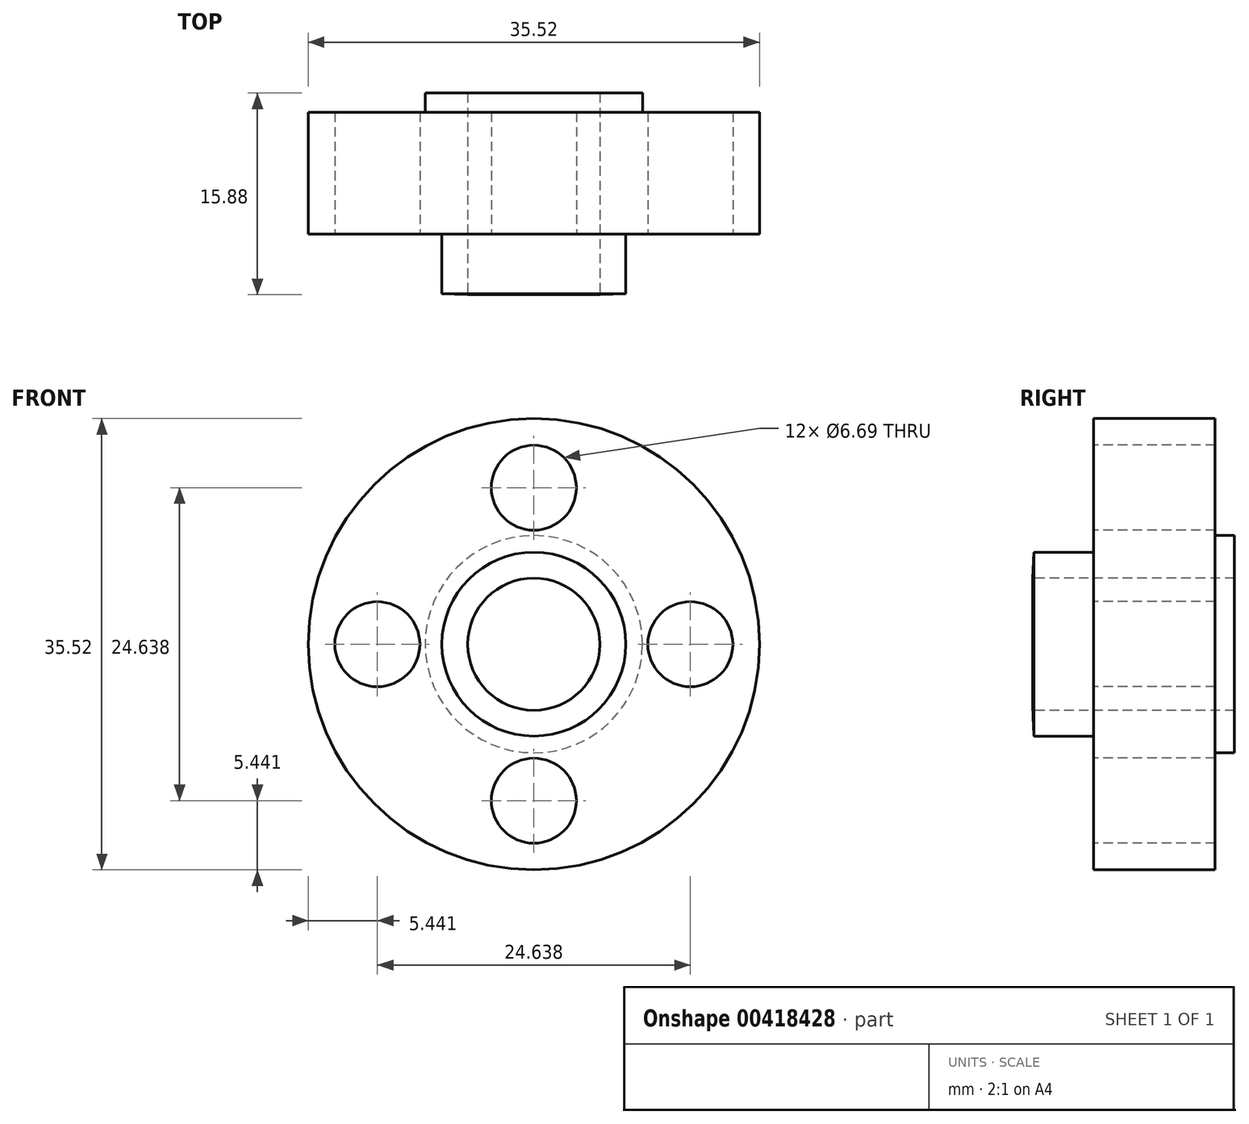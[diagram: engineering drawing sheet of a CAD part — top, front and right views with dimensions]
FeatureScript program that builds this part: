
annotation { "Feature Type Name" : "Feature", "Feature Type Description" : "" }
export const myFeature = defineFeature(function(context is Context, id is Id, definition is map)
    precondition{}
    {
        {
            var Q0;
            Q0=qCreatedBy(makeId("Right.planeOp"),FACE);
            var sketch = newSketch(context, id + "F0", { "sketchPlane" : qUnion([Q0])});
            skLineSegment(sketch, "E0", {"start": v(-29.1, 0) * mm, "end": v(27.48, 0) * mm, "construction": true});
            skLineSegment(sketch, "E1", {"start": v(0, 5.2) * mm, "end": v(15.87, 5.2) * mm});
            skLineSegment(sketch, "E2", {"start": v(15.87, 5.2) * mm, "end": v(15.87, 8.55) * mm});
            skLineSegment(sketch, "E3", {"start": v(15.87, 8.55) * mm, "end": v(14.35, 8.55) * mm});
            skLineSegment(sketch, "E4", {"start": v(14.35, 8.55) * mm, "end": v(14.35, 17.76) * mm});
            skLineSegment(sketch, "E5", {"start": v(14.35, 17.76) * mm, "end": v(4.78, 17.76) * mm});
            skLineSegment(sketch, "E6", {"start": v(4.78, 17.76) * mm, "end": v(4.78, 7.24) * mm});
            skLineSegment(sketch, "E7", {"start": v(4.78, 7.24) * mm, "end": v(0, 7.24) * mm});
            skLineSegment(sketch, "E8", {"start": v(0.09, 7.24) * mm, "end": v(0, 5.2) * mm});
            skSolve(sketch);
        }
        {
            var Q0;
            Q0 = qSketchRegion(id + "F0", true);
            var Q1;
            Q1=sQuery(id+"F0.wireOp",EDGE,"E0");
            revolve(context, id + "F1", {"entities" : qUnion([Q0]), "axis" : qUnion([Q1]), "revolveType" : RevolveType.FULL});
        }
        {
            var Q0;
            Q0=makeQuery(id+"F1.opRevolve","SWEPT_FACE",FACE,{"disambiguationData":[OSD([sQuery(id+"F0.wireOp",EDGE,"E6")])]});
            var sketch = newSketch(context, id + "F2", { "sketchPlane" : qUnion([Q0])});
            skCircle(sketch, "E9", {"center": v(0, 0) * mm, "radius": 12.32 * mm, "construction": true});
            skCircle(sketch, "E10", {"center": v(0, 12.32) * mm, "radius": 3.34 * mm});
            skCircle(sketch, "E11.1.0", {"center": v(-12.32, 0) * mm, "radius": 3.34 * mm});
            skCircle(sketch, "E11.2.0", {"center": v(0, -12.32) * mm, "radius": 3.34 * mm});
            skCircle(sketch, "E11.3.0", {"center": v(12.32, 0) * mm, "radius": 3.34 * mm});
            skSolve(sketch);
        }
        {
            var Q0;
            Q0 = qSketchRegion(id + "F2", true);
            extrude(context, id + "F3", {"entities" : qUnion([Q0]), "operationType" : NewBodyOperationType.REMOVE, "endBound" : BoundingType.THROUGH_ALL, "oppositeDirection" : true, "depth" : 25.4 * mm});
        }
    });
